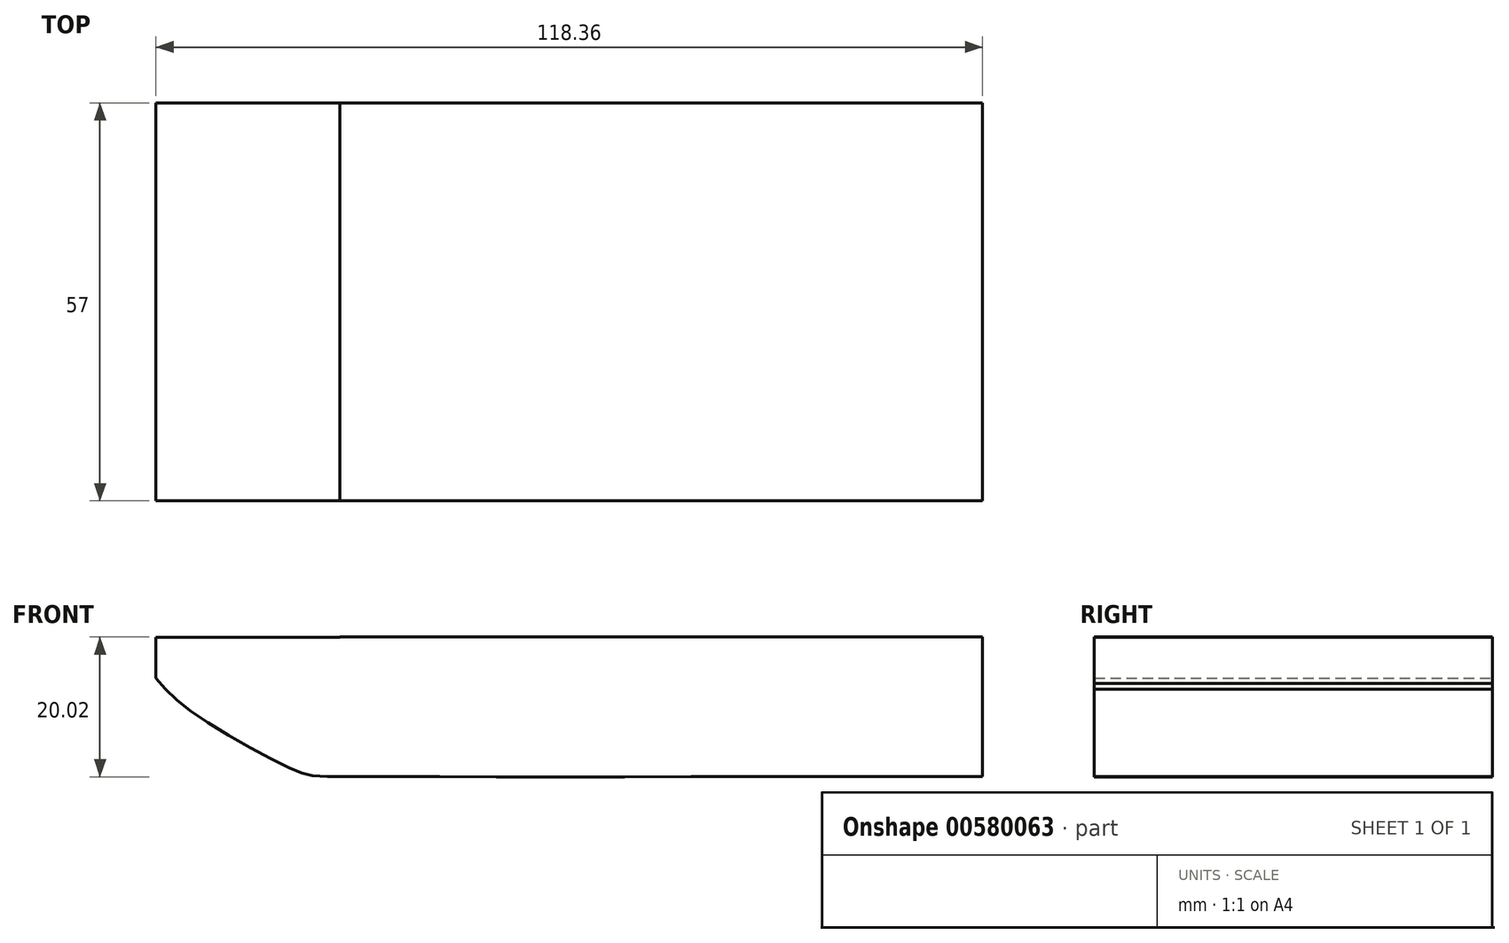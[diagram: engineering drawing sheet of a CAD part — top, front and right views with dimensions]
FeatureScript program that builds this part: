
annotation { "Feature Type Name" : "Feature", "Feature Type Description" : "" }
export const myFeature = defineFeature(function(context is Context, id is Id, definition is map)
    precondition{}
    {
        {
            var Q0;
            Q0=qCreatedBy(makeId("Top.planeOp"),FACE);
            var sketch = newSketch(context, id + "F0", { "sketchPlane" : qUnion([Q0])});
            skLineSegment(sketch, "E0.bottom", {"start": v(46, 28.5) * mm, "end": v(-46, 28.5) * mm});
            skLineSegment(sketch, "E0.top", {"start": v(46, -28.5) * mm, "end": v(-46, -28.5) * mm});
            skLineSegment(sketch, "E0.left", {"start": v(46, 28.5) * mm, "end": v(46, -28.5) * mm});
            skLineSegment(sketch, "E0.right", {"start": v(-46, 28.5) * mm, "end": v(-46, -28.5) * mm});
            skPoint(sketch, "E0.middle", {"position": v(0, 0) * mm});
            skSolve(sketch);
        }
        {
            var Q0;
            Q0 = qSketchRegion(id + "F0", true);
            extrude(context, id + "F1", {"entities" : qUnion([Q0]), "depth" : 20 * mm, "offsetDistance" : 25.4 * mm});
        }
        {
            var Q0;
            Q0=qCreatedBy(makeId("Front.planeOp"),FACE);
            var sketch = newSketch(context, id + "F2", { "sketchPlane" : qUnion([Q0])});
            skLineSegment(sketch, "E1", {"start": v(46.01, 13.37) * mm, "end": v(46.01, 19.97) * mm});
            skLineSegment(sketch, "E2", {"start": v(46.01, 19.97) * mm, "end": v(-72.35, 19.97) * mm});
            skLineSegment(sketch, "E3", {"start": v(-72.35, 19.97) * mm, "end": v(-72.35, 14.12) * mm});
            skFitSpline(sketch, "E4", {"points": [v(-72.35, 14.12) * mm, v(-66.05, 8.48) * mm, v(-52.46, 0.9) * mm, v(-46.14, 0) * mm, v(40.88, 0) * mm, v(45.63, 0.78) * mm, v(45.98, 4.62) * mm, v(46.01, 13.37) * mm], "startDerivative": vector(41.7, -51.7) * mm, "endDerivative": vector(1.12, 55.1) * mm});
            skSolve(sketch);
        }
        {
            var Q0;
            Q0 = qSketchRegion(id + "F2", true);
            extrude(context, id + "F3", {"entities" : qUnion([Q0]), "operationType" : NewBodyOperationType.ADD, "endBound" : BoundingType.SYMMETRIC, "depth" : 57 * mm, "offsetDistance" : 25.4 * mm});
        }
    });
